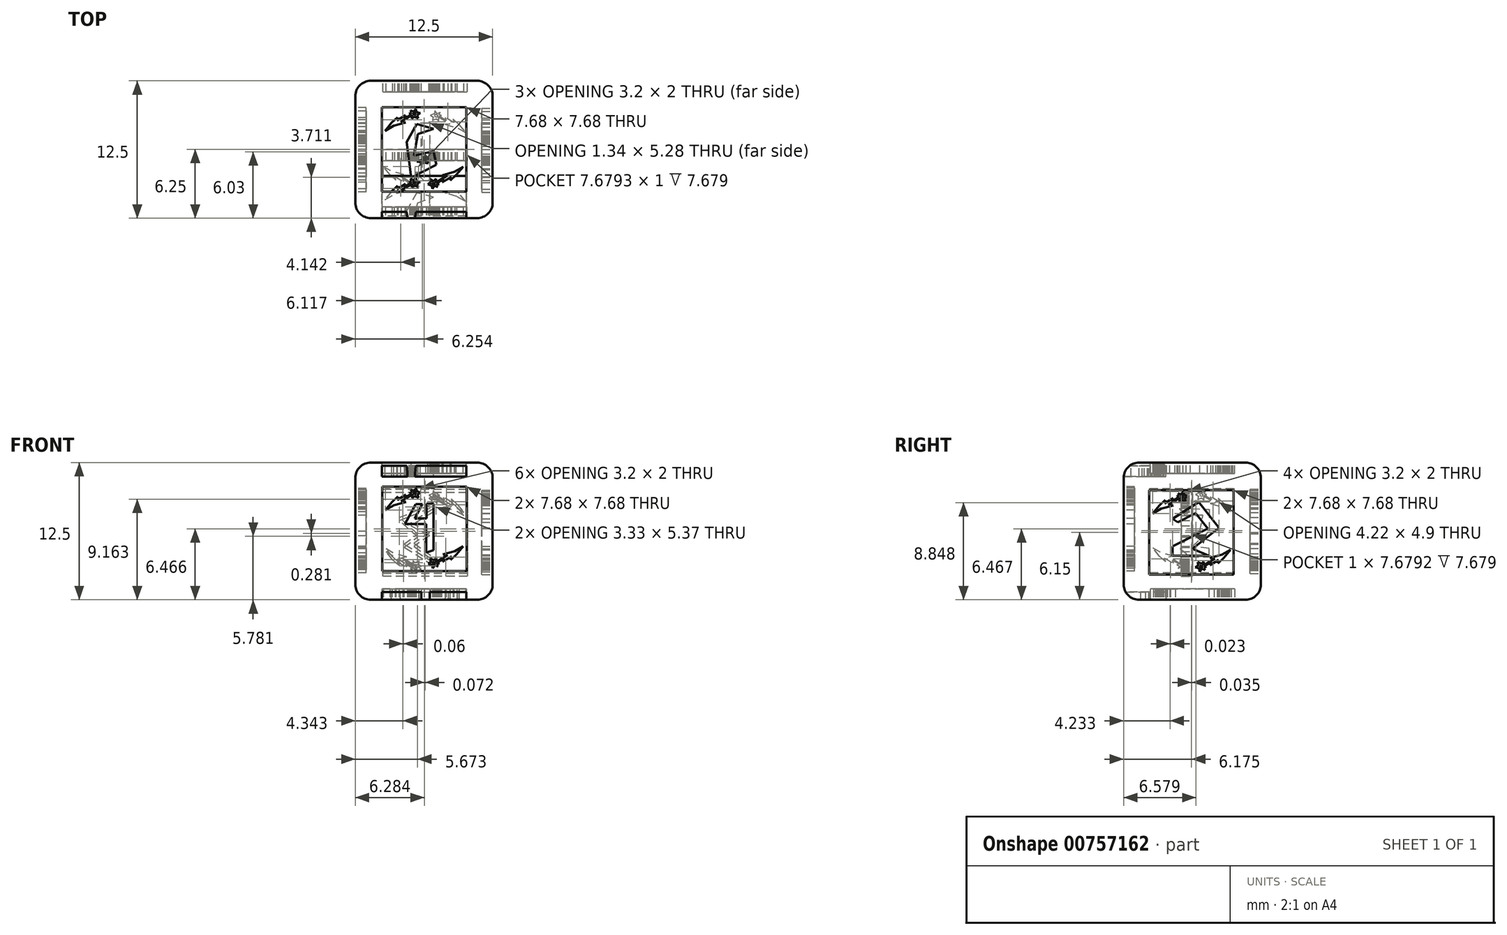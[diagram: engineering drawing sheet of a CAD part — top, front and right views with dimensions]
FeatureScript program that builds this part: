
annotation { "Feature Type Name" : "Feature", "Feature Type Description" : "" }
export const myFeature = defineFeature(function(context is Context, id is Id, definition is map)
    precondition{}
    {
        {
            var Q0;
            Q0=qCreatedBy(makeId("Front.planeOp"),FACE);
            var sketch = newSketch(context, id + "F0", { "sketchPlane" : qUnion([Q0])});
            skLineSegment(sketch, "E0.bottom", {"start": v(-6.25, 5.97) * mm, "end": v(6.25, 5.97) * mm});
            skLineSegment(sketch, "E0.top", {"start": v(-6.25, -6.53) * mm, "end": v(6.25, -6.53) * mm});
            skLineSegment(sketch, "E0.left", {"start": v(-6.25, 5.97) * mm, "end": v(-6.25, -6.53) * mm});
            skLineSegment(sketch, "E0.right", {"start": v(6.25, 5.97) * mm, "end": v(6.25, -6.53) * mm});
            skSolve(sketch);
        }
        {
            var Q0;
            Q0=makeQuery(id+"F0.imprint","IMPRINT",FACE,{"disambiguationData":[TD([[makeQuery(id+"F0.imprint","IMPRINT",EDGE,{"derivedFrom":sQuery(id+"F0.wireOp",EDGE,"E0.bottom")}),-1.0]])]});
            extrude(context, id + "F1", {"entities" : qUnion([Q0]), "depth" : 12.5 * mm, "offsetDistance" : 25.4 * mm});
        }
        {
            var Q0;
            Q0=makeQuery(id+"F1.opExtrude","SWEPT_EDGE",EDGE,{"disambiguationData":[OSD([sQuery(id+"F0.wireOp",EDGE,"E0.bottom"),sQuery(id+"F0.wireOp",EDGE,"E0.left")])]});
            var Q1;
            Q1=makeQuery(id+"F1.opExtrude","SWEPT_FACE",FACE,{"disambiguationData":[OSD([sQuery(id+"F0.wireOp",EDGE,"E0.bottom")])]});
            var Q2;
            Q2=makeQuery(id+"F1.opExtrude","SWEPT_FACE",FACE,{"disambiguationData":[OSD([sQuery(id+"F0.wireOp",EDGE,"E0.top")])]});
            var Q3;
            Q3=makeQuery(id+"F1.opExtrude","CAP_FACE",FACE,{"disambiguationData":[OSD([sQuery(id+"F0.wireOp",EDGE,"E0.bottom"),sQuery(id+"F0.wireOp",EDGE,"E0.top"),sQuery(id+"F0.wireOp",EDGE,"E0.left"),sQuery(id+"F0.wireOp",EDGE,"E0.right")])],"isStart":false});
            var Q4;
            Q4=makeQuery(id+"F1.opExtrude","SWEPT_FACE",FACE,{"disambiguationData":[OSD([sQuery(id+"F0.wireOp",EDGE,"E0.right")])]});
            var Q5;
            Q5=makeQuery(id+"F1.opExtrude","CAP_FACE",FACE,{"disambiguationData":[OSD([sQuery(id+"F0.wireOp",EDGE,"E0.bottom"),sQuery(id+"F0.wireOp",EDGE,"E0.top"),sQuery(id+"F0.wireOp",EDGE,"E0.left"),sQuery(id+"F0.wireOp",EDGE,"E0.right")])],"isStart":true});
            fillet(context, id + "F2", {"entities" : qUnion([Q0, Q1, Q2, Q3, Q4, Q5]), "radius" : 1.41 * mm, "tangentPropagation" : true, "allowEdgeOverflow" : false});
        }
        {
            var Q0;
            Q0=makeQuery(id+"F1.opExtrude","SWEPT_FACE",FACE,{"disambiguationData":[OSD([sQuery(id+"F0.wireOp",EDGE,"E0.bottom")])]});
            var sketch = newSketch(context, id + "F3", { "sketchPlane" : qUnion([Q0])});
            skLineSegment(sketch, "E1.0", {"start": v(3.84, -2.41) * mm, "end": v(-3.84, -2.41) * mm});
            skLineSegment(sketch, "E1.1", {"start": v(3.84, -10.09) * mm, "end": v(3.84, -2.41) * mm});
            skLineSegment(sketch, "E1.2", {"start": v(-3.84, -10.09) * mm, "end": v(3.84, -10.09) * mm});
            skLineSegment(sketch, "E1.3", {"start": v(-3.84, -2.41) * mm, "end": v(-3.84, -10.09) * mm});
            skLineSegment(sketch, "E2", {"start": v(-2.93, -3.8) * mm, "end": v(-2.39, -3.31) * mm});
            skLineSegment(sketch, "E3", {"start": v(-2.39, -3.31) * mm, "end": v(-2.46, -3.62) * mm});
            skLineSegment(sketch, "E4", {"start": v(-2.46, -3.62) * mm, "end": v(-1.66, -3.14) * mm});
            skLineSegment(sketch, "E5", {"start": v(-1.66, -3.14) * mm, "end": v(-1.75, -3.43) * mm});
            skLineSegment(sketch, "E6", {"start": v(-1.75, -3.43) * mm, "end": v(-1.12, -3.06) * mm});
            skLineSegment(sketch, "E7", {"start": v(-1.12, -3.06) * mm, "end": v(-1.35, -3) * mm});
            skLineSegment(sketch, "E8", {"start": v(-1.35, -3) * mm, "end": v(-1.12, -2.88) * mm});
            skLineSegment(sketch, "E9", {"start": v(-1.12, -2.88) * mm, "end": v(-1.22, -2.7) * mm});
            skLineSegment(sketch, "E10", {"start": v(-1.22, -2.7) * mm, "end": v(-0.94, -2.83) * mm});
            skLineSegment(sketch, "E11", {"start": v(-0.94, -2.83) * mm, "end": v(-0.75, -2.55) * mm});
            skLineSegment(sketch, "E12", {"start": v(-0.75, -2.55) * mm, "end": v(-0.68, -2.84) * mm});
            skLineSegment(sketch, "E13", {"start": v(-0.68, -2.84) * mm, "end": v(-0.34, -2.95) * mm});
            skLineSegment(sketch, "E14", {"start": v(-0.34, -2.95) * mm, "end": v(-0.6, -3.12) * mm});
            skLineSegment(sketch, "E15", {"start": v(-0.6, -3.12) * mm, "end": v(-0.54, -3.43) * mm});
            skLineSegment(sketch, "E16", {"start": v(-0.54, -3.43) * mm, "end": v(-0.89, -3.26) * mm});
            skLineSegment(sketch, "E17", {"start": v(-0.89, -3.26) * mm, "end": v(-1.08, -3.47) * mm});
            skLineSegment(sketch, "E18", {"start": v(-1.08, -3.47) * mm, "end": v(-1.08, -3.12) * mm});
            skLineSegment(sketch, "E19", {"start": v(-1.08, -3.12) * mm, "end": v(-2.1, -3.74) * mm});
            skLineSegment(sketch, "E20", {"start": v(-2.1, -3.74) * mm, "end": v(-1.66, -3.8) * mm});
            skLineSegment(sketch, "E21", {"start": v(-1.66, -3.8) * mm, "end": v(-2.75, -4.1) * mm});
            skLineSegment(sketch, "E22", {"start": v(-2.93, -3.8) * mm, "end": v(-3.54, -4.55) * mm});
            skLineSegment(sketch, "E23", {"start": v(-3.54, -4.55) * mm, "end": v(-2.75, -4.1) * mm});
            skLineSegment(sketch, "E24", {"start": v(-0.9, -2.92) * mm, "end": v(-0.77, -2.9) * mm});
            skLineSegment(sketch, "E25", {"start": v(-0.77, -2.9) * mm, "end": v(-0.7, -2.97) * mm});
            skLineSegment(sketch, "E26", {"start": v(-0.7, -2.97) * mm, "end": v(-0.74, -3.08) * mm});
            skLineSegment(sketch, "E27", {"start": v(-0.74, -3.08) * mm, "end": v(-0.9, -3.11) * mm});
            skLineSegment(sketch, "E28", {"start": v(-0.9, -3.11) * mm, "end": v(-1.03, -3.03) * mm});
            skLineSegment(sketch, "E29", {"start": v(-1.03, -3.03) * mm, "end": v(-0.9, -2.92) * mm});
            skLineSegment(sketch, "E30", {"start": v(2.95, -8.58) * mm, "end": v(2.4, -9.07) * mm});
            skLineSegment(sketch, "E31", {"start": v(2.4, -9.07) * mm, "end": v(2.48, -8.76) * mm});
            skLineSegment(sketch, "E32", {"start": v(2.48, -8.76) * mm, "end": v(1.68, -9.24) * mm});
            skLineSegment(sketch, "E33", {"start": v(1.68, -9.24) * mm, "end": v(1.77, -8.96) * mm});
            skLineSegment(sketch, "E34", {"start": v(1.77, -8.96) * mm, "end": v(1.14, -9.33) * mm});
            skLineSegment(sketch, "E35", {"start": v(1.14, -9.33) * mm, "end": v(1.37, -9.38) * mm});
            skLineSegment(sketch, "E36", {"start": v(1.37, -9.38) * mm, "end": v(1.14, -9.5) * mm});
            skLineSegment(sketch, "E37", {"start": v(1.14, -9.5) * mm, "end": v(1.24, -9.69) * mm});
            skLineSegment(sketch, "E38", {"start": v(1.24, -9.69) * mm, "end": v(0.96, -9.56) * mm});
            skLineSegment(sketch, "E39", {"start": v(0.96, -9.56) * mm, "end": v(0.77, -9.83) * mm});
            skLineSegment(sketch, "E40", {"start": v(0.77, -9.83) * mm, "end": v(0.7, -9.54) * mm});
            skLineSegment(sketch, "E41", {"start": v(0.7, -9.54) * mm, "end": v(0.36, -9.43) * mm});
            skLineSegment(sketch, "E42", {"start": v(0.36, -9.43) * mm, "end": v(0.63, -9.26) * mm});
            skLineSegment(sketch, "E43", {"start": v(0.63, -9.26) * mm, "end": v(0.56, -8.95) * mm});
            skLineSegment(sketch, "E44", {"start": v(0.56, -8.95) * mm, "end": v(0.9, -9.12) * mm});
            skLineSegment(sketch, "E45", {"start": v(0.9, -9.12) * mm, "end": v(1.1, -8.92) * mm});
            skLineSegment(sketch, "E46", {"start": v(1.1, -8.92) * mm, "end": v(1.1, -9.27) * mm});
            skLineSegment(sketch, "E47", {"start": v(1.1, -9.27) * mm, "end": v(2.12, -8.64) * mm});
            skLineSegment(sketch, "E48", {"start": v(2.12, -8.64) * mm, "end": v(1.68, -8.59) * mm});
            skLineSegment(sketch, "E49", {"start": v(1.68, -8.59) * mm, "end": v(2.77, -8.3) * mm});
            skLineSegment(sketch, "E50", {"start": v(2.95, -8.58) * mm, "end": v(3.56, -7.83) * mm});
            skLineSegment(sketch, "E51", {"start": v(3.56, -7.83) * mm, "end": v(2.77, -8.3) * mm});
            skLineSegment(sketch, "E52", {"start": v(0.92, -9.47) * mm, "end": v(0.8, -9.49) * mm});
            skLineSegment(sketch, "E53", {"start": v(0.8, -9.49) * mm, "end": v(0.72, -9.41) * mm});
            skLineSegment(sketch, "E54", {"start": v(0.72, -9.41) * mm, "end": v(0.76, -9.3) * mm});
            skLineSegment(sketch, "E55", {"start": v(0.76, -9.3) * mm, "end": v(0.92, -9.27) * mm});
            skLineSegment(sketch, "E56", {"start": v(0.92, -9.27) * mm, "end": v(1.05, -9.35) * mm});
            skLineSegment(sketch, "E57", {"start": v(1.05, -9.35) * mm, "end": v(0.92, -9.47) * mm});
            skLineSegment(sketch, "E58", {"start": v(0.88, -4.36) * mm, "end": v(-0.65, -3.94) * mm});
            skLineSegment(sketch, "E59", {"start": v(-0.65, -3.94) * mm, "end": v(-1.59, -5.58) * mm});
            skLineSegment(sketch, "E60", {"start": v(-1.59, -5.58) * mm, "end": v(-1.17, -8.8) * mm});
            skLineSegment(sketch, "E61", {"start": v(-1.17, -8.8) * mm, "end": v(1.14, -7.65) * mm});
            skLineSegment(sketch, "E62", {"start": v(1.14, -7.65) * mm, "end": v(0.86, -6.41) * mm});
            skLineSegment(sketch, "E63", {"start": v(0.86, -6.41) * mm, "end": v(-0.92, -6.82) * mm});
            skLineSegment(sketch, "E64", {"start": v(-0.92, -6.82) * mm, "end": v(-0.57, -4.86) * mm});
            skLineSegment(sketch, "E65", {"start": v(-0.57, -4.86) * mm, "end": v(0.88, -4.36) * mm});
            skLineSegment(sketch, "E66", {"start": v(0.16, -7.09) * mm, "end": v(-0.66, -7.37) * mm});
            skLineSegment(sketch, "E67", {"start": v(-0.66, -7.37) * mm, "end": v(0.38, -7.53) * mm});
            skLineSegment(sketch, "E68", {"start": v(0.38, -7.53) * mm, "end": v(0.16, -7.09) * mm});
            skSolve(sketch);
        }
        {
            var Q0;
            Q0=makeQuery(id+"F3.imprint","IMPRINT",FACE,{"disambiguationData":[TD([[makeQuery(id+"F3.imprint","IMPRINT",EDGE,{"derivedFrom":sQuery(id+"F3.wireOp",EDGE,"E1.0")}),1.0]])]});
            var Q1;
            Q1=makeQuery(id+"F3.imprint","IMPRINT",FACE,{"disambiguationData":[TD([[makeQuery(id+"F3.imprint","IMPRINT",EDGE,{"derivedFrom":sQuery(id+"F3.wireOp",EDGE,"ba902a5d-1331-4e5e-a22d-ac149d70c835.sketch_text.stroke-17")}),1.0]])]});
            var Q2;
            Q2=makeQuery(id+"F3.imprint","IMPRINT",FACE,{"disambiguationData":[TD([[makeQuery(id+"F3.imprint","IMPRINT",EDGE,{"derivedFrom":sQuery(id+"F3.wireOp",EDGE,"E52")}),-1.0]])]});
            var Q3;
            Q3=makeQuery(id+"F3.imprint","IMPRINT",FACE,{"disambiguationData":[TD([[makeQuery(id+"F3.imprint","IMPRINT",EDGE,{"derivedFrom":sQuery(id+"F3.wireOp",EDGE,"E24")}),-1.0]])]});
            var Q4;
            Q4=makeQuery(id+"F3.imprint","IMPRINT",FACE,{"disambiguationData":[TD([[makeQuery(id+"F3.imprint","IMPRINT",EDGE,{"derivedFrom":sQuery(id+"F3.wireOp",EDGE,"E66")}),1.0]])]});
            extrude(context, id + "F4", {"entities" : qUnion([Q0, Q1, Q2, Q3, Q4]), "operationType" : NewBodyOperationType.REMOVE, "oppositeDirection" : true, "depth" : 1 * mm, "offsetDistance" : 25.4 * mm});
        }
        {
            var Q0;
            Q0=makeQuery(id+"F1.opExtrude","CAP_FACE",FACE,{"disambiguationData":[OSD([sQuery(id+"F0.wireOp",EDGE,"E0.bottom"),sQuery(id+"F0.wireOp",EDGE,"E0.top"),sQuery(id+"F0.wireOp",EDGE,"E0.left"),sQuery(id+"F0.wireOp",EDGE,"E0.right")])],"isStart":true});
            var sketch = newSketch(context, id + "F5", { "sketchPlane" : qUnion([Q0])});
            skLineSegment(sketch, "E69.0", {"start": v(3.73, 3.56) * mm, "end": v(-3.95, 3.56) * mm});
            skLineSegment(sketch, "E69.1", {"start": v(3.73, -4.12) * mm, "end": v(3.73, 3.56) * mm});
            skLineSegment(sketch, "E69.2", {"start": v(-3.95, -4.12) * mm, "end": v(3.73, -4.12) * mm});
            skLineSegment(sketch, "E69.3", {"start": v(-3.95, 3.56) * mm, "end": v(-3.95, -4.12) * mm});
            skLineSegment(sketch, "E70", {"start": v(-3.04, 2.16) * mm, "end": v(-2.5, 2.65) * mm});
            skLineSegment(sketch, "E71", {"start": v(-2.5, 2.65) * mm, "end": v(-2.57, 2.34) * mm});
            skLineSegment(sketch, "E72", {"start": v(-2.57, 2.34) * mm, "end": v(-1.77, 2.82) * mm});
            skLineSegment(sketch, "E73", {"start": v(-1.77, 2.82) * mm, "end": v(-1.86, 2.54) * mm});
            skLineSegment(sketch, "E74", {"start": v(-1.86, 2.54) * mm, "end": v(-1.23, 2.9) * mm});
            skLineSegment(sketch, "E75", {"start": v(-1.23, 2.9) * mm, "end": v(-1.46, 2.96) * mm});
            skLineSegment(sketch, "E76", {"start": v(-1.46, 2.96) * mm, "end": v(-1.23, 3.08) * mm});
            skLineSegment(sketch, "E77", {"start": v(-1.23, 3.08) * mm, "end": v(-1.33, 3.27) * mm});
            skLineSegment(sketch, "E78", {"start": v(-1.33, 3.27) * mm, "end": v(-1.05, 3.14) * mm});
            skLineSegment(sketch, "E79", {"start": v(-1.05, 3.14) * mm, "end": v(-0.86, 3.42) * mm});
            skLineSegment(sketch, "E80", {"start": v(-0.86, 3.42) * mm, "end": v(-0.8, 3.13) * mm});
            skLineSegment(sketch, "E81", {"start": v(-0.8, 3.13) * mm, "end": v(-0.45, 3.01) * mm});
            skLineSegment(sketch, "E82", {"start": v(-0.45, 3.01) * mm, "end": v(-0.72, 2.85) * mm});
            skLineSegment(sketch, "E83", {"start": v(-0.72, 2.85) * mm, "end": v(-0.65, 2.53) * mm});
            skLineSegment(sketch, "E84", {"start": v(-0.65, 2.53) * mm, "end": v(-1, 2.7) * mm});
            skLineSegment(sketch, "E85", {"start": v(-1, 2.7) * mm, "end": v(-1.2, 2.5) * mm});
            skLineSegment(sketch, "E86", {"start": v(-1.2, 2.5) * mm, "end": v(-1.2, 2.85) * mm});
            skLineSegment(sketch, "E87", {"start": v(-1.2, 2.85) * mm, "end": v(-2.2, 2.22) * mm});
            skLineSegment(sketch, "E88", {"start": v(-2.2, 2.22) * mm, "end": v(-1.77, 2.17) * mm});
            skLineSegment(sketch, "E89", {"start": v(-1.77, 2.17) * mm, "end": v(-2.86, 1.87) * mm});
            skLineSegment(sketch, "E90", {"start": v(-3.04, 2.16) * mm, "end": v(-3.65, 1.41) * mm});
            skLineSegment(sketch, "E91", {"start": v(-3.65, 1.41) * mm, "end": v(-2.86, 1.87) * mm});
            skLineSegment(sketch, "E92", {"start": v(-1.01, 3.05) * mm, "end": v(-0.88, 3.07) * mm});
            skLineSegment(sketch, "E93", {"start": v(-0.88, 3.07) * mm, "end": v(-0.81, 3) * mm});
            skLineSegment(sketch, "E94", {"start": v(-0.81, 3) * mm, "end": v(-0.85, 2.88) * mm});
            skLineSegment(sketch, "E95", {"start": v(-0.85, 2.88) * mm, "end": v(-1, 2.86) * mm});
            skLineSegment(sketch, "E96", {"start": v(-1, 2.86) * mm, "end": v(-1.14, 2.94) * mm});
            skLineSegment(sketch, "E97", {"start": v(-1.14, 2.94) * mm, "end": v(-1.01, 3.05) * mm});
            skLineSegment(sketch, "E98", {"start": v(2.84, -2.61) * mm, "end": v(2.3, -3.1) * mm});
            skLineSegment(sketch, "E99", {"start": v(2.3, -3.1) * mm, "end": v(2.37, -2.8) * mm});
            skLineSegment(sketch, "E100", {"start": v(2.37, -2.8) * mm, "end": v(1.57, -3.27) * mm});
            skLineSegment(sketch, "E101", {"start": v(1.57, -3.27) * mm, "end": v(1.66, -3) * mm});
            skLineSegment(sketch, "E102", {"start": v(1.66, -3) * mm, "end": v(1.03, -3.36) * mm});
            skLineSegment(sketch, "E103", {"start": v(1.03, -3.36) * mm, "end": v(1.26, -3.41) * mm});
            skLineSegment(sketch, "E104", {"start": v(1.26, -3.41) * mm, "end": v(1.03, -3.53) * mm});
            skLineSegment(sketch, "E105", {"start": v(1.03, -3.53) * mm, "end": v(1.13, -3.72) * mm});
            skLineSegment(sketch, "E106", {"start": v(1.13, -3.72) * mm, "end": v(0.85, -3.6) * mm});
            skLineSegment(sketch, "E107", {"start": v(0.85, -3.6) * mm, "end": v(0.66, -3.87) * mm});
            skLineSegment(sketch, "E108", {"start": v(0.66, -3.87) * mm, "end": v(0.6, -3.58) * mm});
            skLineSegment(sketch, "E109", {"start": v(0.6, -3.58) * mm, "end": v(0.25, -3.46) * mm});
            skLineSegment(sketch, "E110", {"start": v(0.25, -3.46) * mm, "end": v(0.52, -3.3) * mm});
            skLineSegment(sketch, "E111", {"start": v(0.52, -3.3) * mm, "end": v(0.45, -2.98) * mm});
            skLineSegment(sketch, "E112", {"start": v(0.45, -2.98) * mm, "end": v(0.8, -3.15) * mm});
            skLineSegment(sketch, "E113", {"start": v(0.8, -3.15) * mm, "end": v(1, -2.95) * mm});
            skLineSegment(sketch, "E114", {"start": v(1, -2.95) * mm, "end": v(1, -3.3) * mm});
            skLineSegment(sketch, "E115", {"start": v(1, -3.3) * mm, "end": v(2, -2.67) * mm});
            skLineSegment(sketch, "E116", {"start": v(2, -2.67) * mm, "end": v(1.57, -2.62) * mm});
            skLineSegment(sketch, "E117", {"start": v(1.57, -2.62) * mm, "end": v(2.66, -2.32) * mm});
            skLineSegment(sketch, "E118", {"start": v(2.84, -2.61) * mm, "end": v(3.45, -1.86) * mm});
            skLineSegment(sketch, "E119", {"start": v(3.45, -1.86) * mm, "end": v(2.66, -2.32) * mm});
            skLineSegment(sketch, "E120", {"start": v(0.81, -3.5) * mm, "end": v(0.68, -3.52) * mm});
            skLineSegment(sketch, "E121", {"start": v(0.68, -3.52) * mm, "end": v(0.61, -3.44) * mm});
            skLineSegment(sketch, "E122", {"start": v(0.61, -3.44) * mm, "end": v(0.65, -3.33) * mm});
            skLineSegment(sketch, "E123", {"start": v(0.65, -3.33) * mm, "end": v(0.8, -3.3) * mm});
            skLineSegment(sketch, "E124", {"start": v(0.8, -3.3) * mm, "end": v(0.94, -3.38) * mm});
            skLineSegment(sketch, "E125", {"start": v(0.94, -3.38) * mm, "end": v(0.81, -3.5) * mm});
            skLineSegment(sketch, "E126", {"start": v(-0.85, 2.22) * mm, "end": v(-0.85, 1.73) * mm});
            skLineSegment(sketch, "E127", {"start": v(-0.85, 1.73) * mm, "end": v(1.2, 0.48) * mm});
            skLineSegment(sketch, "E128", {"start": v(1.2, 0.48) * mm, "end": v(-0.53, -0.4) * mm});
            skLineSegment(sketch, "E129", {"start": v(-0.53, -0.4) * mm, "end": v(0.91, -1.38) * mm});
            skLineSegment(sketch, "E130", {"start": v(0.91, -1.38) * mm, "end": v(-1.1, -2.81) * mm});
            skLineSegment(sketch, "E131", {"start": v(-1.1, -2.81) * mm, "end": v(-0.85, -3.15) * mm});
            skLineSegment(sketch, "E132", {"start": v(-0.85, -3.15) * mm, "end": v(1.84, -1.46) * mm});
            skLineSegment(sketch, "E133", {"start": v(1.84, -1.46) * mm, "end": v(0.58, -0.53) * mm});
            skLineSegment(sketch, "E134", {"start": v(0.58, -0.53) * mm, "end": v(2.24, 0.96) * mm});
            skLineSegment(sketch, "E135", {"start": v(2.24, 0.96) * mm, "end": v(-0.85, 2.22) * mm});
            skSolve(sketch);
        }
        {
            var Q0;
            Q0=makeQuery(id+"F5.imprint","IMPRINT",FACE,{"disambiguationData":[TD([[makeQuery(id+"F5.imprint","IMPRINT",EDGE,{"derivedFrom":sQuery(id+"F5.wireOp",EDGE,"E92")}),-1.0]])]});
            var Q1;
            Q1=makeQuery(id+"F5.imprint","IMPRINT",FACE,{"disambiguationData":[TD([[makeQuery(id+"F5.imprint","IMPRINT",EDGE,{"derivedFrom":sQuery(id+"F5.wireOp",EDGE,"E69.0")}),1.0]])]});
            var Q2;
            Q2=makeQuery(id+"F5.imprint","IMPRINT",FACE,{"disambiguationData":[TD([[makeQuery(id+"F5.imprint","IMPRINT",EDGE,{"derivedFrom":sQuery(id+"F5.wireOp",EDGE,"E120")}),-1.0]])]});
            extrude(context, id + "F6", {"entities" : qUnion([Q0, Q1, Q2]), "operationType" : NewBodyOperationType.REMOVE, "oppositeDirection" : true, "depth" : 1 * mm, "offsetDistance" : 25.4 * mm});
        }
        {
            var Q0;
            Q0=makeQuery(id+"F1.opExtrude","SWEPT_FACE",FACE,{"disambiguationData":[OSD([sQuery(id+"F0.wireOp",EDGE,"E0.top")])]});
            var sketch = newSketch(context, id + "F7", { "sketchPlane" : qUnion([Q0])});
            skLineSegment(sketch, "E136.0", {"start": v(3.84, 10.09) * mm, "end": v(-3.84, 10.09) * mm});
            skLineSegment(sketch, "E136.1", {"start": v(3.84, 2.41) * mm, "end": v(3.84, 10.09) * mm});
            skLineSegment(sketch, "E136.2", {"start": v(-3.84, 2.41) * mm, "end": v(3.84, 2.41) * mm});
            skLineSegment(sketch, "E136.3", {"start": v(-3.84, 10.09) * mm, "end": v(-3.84, 2.41) * mm});
            skLineSegment(sketch, "E137", {"start": v(-3.1, 8.53) * mm, "end": v(-2.56, 9.03) * mm});
            skLineSegment(sketch, "E138", {"start": v(-2.56, 9.03) * mm, "end": v(-2.63, 8.72) * mm});
            skLineSegment(sketch, "E139", {"start": v(-2.63, 8.72) * mm, "end": v(-1.83, 9.2) * mm});
            skLineSegment(sketch, "E140", {"start": v(-1.83, 9.2) * mm, "end": v(-1.92, 8.92) * mm});
            skLineSegment(sketch, "E141", {"start": v(-1.92, 8.92) * mm, "end": v(-1.3, 9.28) * mm});
            skLineSegment(sketch, "E142", {"start": v(-1.3, 9.28) * mm, "end": v(-1.52, 9.34) * mm});
            skLineSegment(sketch, "E143", {"start": v(-1.52, 9.34) * mm, "end": v(-1.3, 9.46) * mm});
            skLineSegment(sketch, "E144", {"start": v(-1.3, 9.46) * mm, "end": v(-1.4, 9.65) * mm});
            skLineSegment(sketch, "E145", {"start": v(-1.4, 9.65) * mm, "end": v(-1.11, 9.51) * mm});
            skLineSegment(sketch, "E146", {"start": v(-1.11, 9.51) * mm, "end": v(-0.92, 9.79) * mm});
            skLineSegment(sketch, "E147", {"start": v(-0.92, 9.79) * mm, "end": v(-0.85, 9.5) * mm});
            skLineSegment(sketch, "E148", {"start": v(-0.85, 9.5) * mm, "end": v(-0.5, 9.39) * mm});
            skLineSegment(sketch, "E149", {"start": v(-0.5, 9.39) * mm, "end": v(-0.78, 9.22) * mm});
            skLineSegment(sketch, "E150", {"start": v(-0.78, 9.22) * mm, "end": v(-0.7, 8.9) * mm});
            skLineSegment(sketch, "E151", {"start": v(-0.7, 8.9) * mm, "end": v(-1.06, 9.08) * mm});
            skLineSegment(sketch, "E152", {"start": v(-1.06, 9.08) * mm, "end": v(-1.26, 8.87) * mm});
            skLineSegment(sketch, "E153", {"start": v(-1.26, 8.87) * mm, "end": v(-1.26, 9.23) * mm});
            skLineSegment(sketch, "E154", {"start": v(-1.26, 9.23) * mm, "end": v(-2.27, 8.6) * mm});
            skLineSegment(sketch, "E155", {"start": v(-2.27, 8.6) * mm, "end": v(-1.83, 8.54) * mm});
            skLineSegment(sketch, "E156", {"start": v(-1.83, 8.54) * mm, "end": v(-2.92, 8.25) * mm});
            skLineSegment(sketch, "E157", {"start": v(-3.1, 8.53) * mm, "end": v(-3.7, 7.79) * mm});
            skLineSegment(sketch, "E158", {"start": v(-3.7, 7.79) * mm, "end": v(-2.92, 8.25) * mm});
            skLineSegment(sketch, "E159", {"start": v(-1.08, 9.43) * mm, "end": v(-0.94, 9.45) * mm});
            skLineSegment(sketch, "E160", {"start": v(-0.94, 9.45) * mm, "end": v(-0.87, 9.37) * mm});
            skLineSegment(sketch, "E161", {"start": v(-0.87, 9.37) * mm, "end": v(-0.91, 9.26) * mm});
            skLineSegment(sketch, "E162", {"start": v(-0.91, 9.26) * mm, "end": v(-1.07, 9.23) * mm});
            skLineSegment(sketch, "E163", {"start": v(-1.07, 9.23) * mm, "end": v(-1.2, 9.3) * mm});
            skLineSegment(sketch, "E164", {"start": v(-1.2, 9.3) * mm, "end": v(-1.08, 9.43) * mm});
            skLineSegment(sketch, "E165", {"start": v(3.18, 3.98) * mm, "end": v(2.64, 3.49) * mm});
            skLineSegment(sketch, "E166", {"start": v(2.64, 3.49) * mm, "end": v(2.71, 3.8) * mm});
            skLineSegment(sketch, "E167", {"start": v(2.71, 3.8) * mm, "end": v(1.9, 3.32) * mm});
            skLineSegment(sketch, "E168", {"start": v(1.9, 3.32) * mm, "end": v(2, 3.6) * mm});
            skLineSegment(sketch, "E169", {"start": v(2, 3.6) * mm, "end": v(1.37, 3.23) * mm});
            skLineSegment(sketch, "E170", {"start": v(1.37, 3.23) * mm, "end": v(1.6, 3.18) * mm});
            skLineSegment(sketch, "E171", {"start": v(1.6, 3.18) * mm, "end": v(1.37, 3.06) * mm});
            skLineSegment(sketch, "E172", {"start": v(1.37, 3.06) * mm, "end": v(1.47, 2.87) * mm});
            skLineSegment(sketch, "E173", {"start": v(1.47, 2.87) * mm, "end": v(1.2, 3) * mm});
            skLineSegment(sketch, "E174", {"start": v(1.2, 3) * mm, "end": v(1, 2.73) * mm});
            skLineSegment(sketch, "E175", {"start": v(1, 2.73) * mm, "end": v(0.93, 3.01) * mm});
            skLineSegment(sketch, "E176", {"start": v(0.93, 3.01) * mm, "end": v(0.59, 3.13) * mm});
            skLineSegment(sketch, "E177", {"start": v(0.59, 3.13) * mm, "end": v(0.86, 3.3) * mm});
            skLineSegment(sketch, "E178", {"start": v(0.86, 3.3) * mm, "end": v(0.79, 3.6) * mm});
            skLineSegment(sketch, "E179", {"start": v(0.79, 3.6) * mm, "end": v(1.14, 3.44) * mm});
            skLineSegment(sketch, "E180", {"start": v(1.14, 3.44) * mm, "end": v(1.34, 3.64) * mm});
            skLineSegment(sketch, "E181", {"start": v(1.34, 3.64) * mm, "end": v(1.34, 3.29) * mm});
            skLineSegment(sketch, "E182", {"start": v(1.34, 3.29) * mm, "end": v(2.35, 3.92) * mm});
            skLineSegment(sketch, "E183", {"start": v(2.35, 3.92) * mm, "end": v(1.91, 3.97) * mm});
            skLineSegment(sketch, "E184", {"start": v(1.91, 3.97) * mm, "end": v(3, 4.27) * mm});
            skLineSegment(sketch, "E185", {"start": v(3.18, 3.98) * mm, "end": v(3.79, 4.73) * mm});
            skLineSegment(sketch, "E186", {"start": v(3.79, 4.73) * mm, "end": v(3, 4.27) * mm});
            skLineSegment(sketch, "E187", {"start": v(1.16, 3.09) * mm, "end": v(1.02, 3.07) * mm});
            skLineSegment(sketch, "E188", {"start": v(1.02, 3.07) * mm, "end": v(0.95, 3.15) * mm});
            skLineSegment(sketch, "E189", {"start": v(0.95, 3.15) * mm, "end": v(1, 3.26) * mm});
            skLineSegment(sketch, "E190", {"start": v(1, 3.26) * mm, "end": v(1.15, 3.29) * mm});
            skLineSegment(sketch, "E191", {"start": v(1.15, 3.29) * mm, "end": v(1.28, 3.2) * mm});
            skLineSegment(sketch, "E192", {"start": v(1.28, 3.2) * mm, "end": v(1.16, 3.09) * mm});
            skLineSegment(sketch, "E193", {"start": v(-0.8, 8.3) * mm, "end": v(-0.23, 8.3) * mm});
            skLineSegment(sketch, "E194", {"start": v(-0.23, 8.3) * mm, "end": v(-0.23, 3.83) * mm});
            skLineSegment(sketch, "E195", {"start": v(-0.23, 3.83) * mm, "end": v(0.54, 3.83) * mm});
            skLineSegment(sketch, "E196", {"start": v(0.54, 3.83) * mm, "end": v(0.54, 9.1) * mm});
            skLineSegment(sketch, "E197", {"start": v(0.54, 9.1) * mm, "end": v(0, 9.1) * mm});
            skLineSegment(sketch, "E198", {"start": v(0, 9.1) * mm, "end": v(-0.8, 8.3) * mm});
            skSolve(sketch);
        }
        {
            var Q0;
            Q0=makeQuery(id+"F7.imprint","IMPRINT",FACE,{"disambiguationData":[TD([[makeQuery(id+"F7.imprint","IMPRINT",EDGE,{"derivedFrom":sQuery(id+"F7.wireOp",EDGE,"E136.0")}),1.0]])]});
            var Q1;
            Q1=makeQuery(id+"F7.imprint","IMPRINT",FACE,{"disambiguationData":[TD([[makeQuery(id+"F7.imprint","IMPRINT",EDGE,{"derivedFrom":sQuery(id+"F7.wireOp",EDGE,"E159")}),-1.0]])]});
            var Q2;
            Q2=makeQuery(id+"F7.imprint","IMPRINT",FACE,{"disambiguationData":[TD([[makeQuery(id+"F7.imprint","IMPRINT",EDGE,{"derivedFrom":sQuery(id+"F7.wireOp",EDGE,"E187")}),-1.0]])]});
            extrude(context, id + "F8", {"entities" : qUnion([Q0, Q1, Q2]), "operationType" : NewBodyOperationType.REMOVE, "oppositeDirection" : true, "depth" : 1 * mm, "offsetDistance" : 25.4 * mm});
        }
        {
            var Q0;
            Q0=makeQuery(id+"F1.opExtrude","CAP_FACE",FACE,{"disambiguationData":[OSD([sQuery(id+"F0.wireOp",EDGE,"E0.bottom"),sQuery(id+"F0.wireOp",EDGE,"E0.top"),sQuery(id+"F0.wireOp",EDGE,"E0.left"),sQuery(id+"F0.wireOp",EDGE,"E0.right")])],"isStart":false});
            var sketch = newSketch(context, id + "F9", { "sketchPlane" : qUnion([Q0])});
            skLineSegment(sketch, "E199.0", {"start": v(3.87, 3.78) * mm, "end": v(-3.8, 3.78) * mm});
            skLineSegment(sketch, "E199.1", {"start": v(3.87, -3.9) * mm, "end": v(3.87, 3.78) * mm});
            skLineSegment(sketch, "E199.2", {"start": v(-3.8, -3.9) * mm, "end": v(3.87, -3.9) * mm});
            skLineSegment(sketch, "E199.3", {"start": v(-3.8, 3.78) * mm, "end": v(-3.8, -3.9) * mm});
            skLineSegment(sketch, "E200", {"start": v(-2.9, 2.38) * mm, "end": v(-2.36, 2.87) * mm});
            skLineSegment(sketch, "E201", {"start": v(-2.36, 2.87) * mm, "end": v(-2.43, 2.56) * mm});
            skLineSegment(sketch, "E202", {"start": v(-2.43, 2.56) * mm, "end": v(-1.62, 3.04) * mm});
            skLineSegment(sketch, "E203", {"start": v(-1.62, 3.04) * mm, "end": v(-1.72, 2.76) * mm});
            skLineSegment(sketch, "E204", {"start": v(-1.72, 2.76) * mm, "end": v(-1.09, 3.13) * mm});
            skLineSegment(sketch, "E205", {"start": v(-1.09, 3.13) * mm, "end": v(-1.31, 3.18) * mm});
            skLineSegment(sketch, "E206", {"start": v(-1.31, 3.18) * mm, "end": v(-1.09, 3.3) * mm});
            skLineSegment(sketch, "E207", {"start": v(-1.09, 3.3) * mm, "end": v(-1.19, 3.49) * mm});
            skLineSegment(sketch, "E208", {"start": v(-1.19, 3.49) * mm, "end": v(-0.91, 3.36) * mm});
            skLineSegment(sketch, "E209", {"start": v(-0.91, 3.36) * mm, "end": v(-0.72, 3.63) * mm});
            skLineSegment(sketch, "E210", {"start": v(-0.72, 3.63) * mm, "end": v(-0.65, 3.34) * mm});
            skLineSegment(sketch, "E211", {"start": v(-0.65, 3.34) * mm, "end": v(-0.3, 3.23) * mm});
            skLineSegment(sketch, "E212", {"start": v(-0.3, 3.23) * mm, "end": v(-0.58, 3.06) * mm});
            skLineSegment(sketch, "E213", {"start": v(-0.58, 3.06) * mm, "end": v(-0.5, 2.75) * mm});
            skLineSegment(sketch, "E214", {"start": v(-0.5, 2.75) * mm, "end": v(-0.86, 2.92) * mm});
            skLineSegment(sketch, "E215", {"start": v(-0.86, 2.92) * mm, "end": v(-1.05, 2.72) * mm});
            skLineSegment(sketch, "E216", {"start": v(-1.05, 2.72) * mm, "end": v(-1.05, 3.07) * mm});
            skLineSegment(sketch, "E217", {"start": v(-1.05, 3.07) * mm, "end": v(-2.07, 2.44) * mm});
            skLineSegment(sketch, "E218", {"start": v(-2.07, 2.44) * mm, "end": v(-1.63, 2.39) * mm});
            skLineSegment(sketch, "E219", {"start": v(-1.63, 2.39) * mm, "end": v(-2.72, 2.1) * mm});
            skLineSegment(sketch, "E220", {"start": v(-2.9, 2.38) * mm, "end": v(-3.5, 1.63) * mm});
            skLineSegment(sketch, "E221", {"start": v(-3.5, 1.63) * mm, "end": v(-2.72, 2.1) * mm});
            skLineSegment(sketch, "E222", {"start": v(-0.87, 3.27) * mm, "end": v(-0.74, 3.29) * mm});
            skLineSegment(sketch, "E223", {"start": v(-0.74, 3.29) * mm, "end": v(-0.67, 3.21) * mm});
            skLineSegment(sketch, "E224", {"start": v(-0.67, 3.21) * mm, "end": v(-0.71, 3.1) * mm});
            skLineSegment(sketch, "E225", {"start": v(-0.71, 3.1) * mm, "end": v(-0.87, 3.07) * mm});
            skLineSegment(sketch, "E226", {"start": v(-0.87, 3.07) * mm, "end": v(-1, 3.15) * mm});
            skLineSegment(sketch, "E227", {"start": v(-1, 3.15) * mm, "end": v(-0.87, 3.27) * mm});
            skLineSegment(sketch, "E228", {"start": v(2.98, -2.4) * mm, "end": v(2.44, -2.89) * mm});
            skLineSegment(sketch, "E229", {"start": v(2.44, -2.89) * mm, "end": v(2.5, -2.58) * mm});
            skLineSegment(sketch, "E230", {"start": v(2.5, -2.58) * mm, "end": v(1.7, -3.06) * mm});
            skLineSegment(sketch, "E231", {"start": v(1.7, -3.06) * mm, "end": v(1.8, -2.77) * mm});
            skLineSegment(sketch, "E232", {"start": v(1.8, -2.77) * mm, "end": v(1.17, -3.14) * mm});
            skLineSegment(sketch, "E233", {"start": v(1.17, -3.14) * mm, "end": v(1.4, -3.2) * mm});
            skLineSegment(sketch, "E234", {"start": v(1.4, -3.2) * mm, "end": v(1.17, -3.32) * mm});
            skLineSegment(sketch, "E235", {"start": v(1.17, -3.32) * mm, "end": v(1.27, -3.5) * mm});
            skLineSegment(sketch, "E236", {"start": v(1.27, -3.5) * mm, "end": v(1, -3.37) * mm});
            skLineSegment(sketch, "E237", {"start": v(1, -3.37) * mm, "end": v(0.8, -3.65) * mm});
            skLineSegment(sketch, "E238", {"start": v(0.8, -3.65) * mm, "end": v(0.73, -3.36) * mm});
            skLineSegment(sketch, "E239", {"start": v(0.73, -3.36) * mm, "end": v(0.39, -3.25) * mm});
            skLineSegment(sketch, "E240", {"start": v(0.39, -3.25) * mm, "end": v(0.66, -3.08) * mm});
            skLineSegment(sketch, "E241", {"start": v(0.66, -3.08) * mm, "end": v(0.59, -2.77) * mm});
            skLineSegment(sketch, "E242", {"start": v(0.59, -2.77) * mm, "end": v(0.94, -2.94) * mm});
            skLineSegment(sketch, "E243", {"start": v(0.94, -2.94) * mm, "end": v(1.14, -2.73) * mm});
            skLineSegment(sketch, "E244", {"start": v(1.14, -2.73) * mm, "end": v(1.14, -3.08) * mm});
            skLineSegment(sketch, "E245", {"start": v(1.14, -3.08) * mm, "end": v(2.15, -2.46) * mm});
            skLineSegment(sketch, "E246", {"start": v(2.15, -2.46) * mm, "end": v(1.71, -2.4) * mm});
            skLineSegment(sketch, "E247", {"start": v(1.71, -2.4) * mm, "end": v(2.8, -2.1) * mm});
            skLineSegment(sketch, "E248", {"start": v(2.98, -2.4) * mm, "end": v(3.59, -1.65) * mm});
            skLineSegment(sketch, "E249", {"start": v(3.59, -1.65) * mm, "end": v(2.8, -2.1) * mm});
            skLineSegment(sketch, "E250", {"start": v(0.95, -3.28) * mm, "end": v(0.82, -3.3) * mm});
            skLineSegment(sketch, "E251", {"start": v(0.82, -3.3) * mm, "end": v(0.75, -3.23) * mm});
            skLineSegment(sketch, "E252", {"start": v(0.75, -3.23) * mm, "end": v(0.8, -3.11) * mm});
            skLineSegment(sketch, "E253", {"start": v(0.8, -3.11) * mm, "end": v(0.95, -3.09) * mm});
            skLineSegment(sketch, "E254", {"start": v(0.95, -3.09) * mm, "end": v(1.08, -3.17) * mm});
            skLineSegment(sketch, "E255", {"start": v(1.08, -3.17) * mm, "end": v(0.95, -3.28) * mm});
            skLineSegment(sketch, "E256", {"start": v(-0.75, 2.17) * mm, "end": v(-1.74, 0.37) * mm});
            skLineSegment(sketch, "E257", {"start": v(-1.74, 0.37) * mm, "end": v(0.2, 0.37) * mm});
            skLineSegment(sketch, "E258", {"start": v(0.2, 0.37) * mm, "end": v(0.2, -2.22) * mm});
            skLineSegment(sketch, "E259", {"start": v(0.2, -2.22) * mm, "end": v(0.87, -2.01) * mm});
            skLineSegment(sketch, "E260", {"start": v(0.87, -2.01) * mm, "end": v(0.87, 2.22) * mm});
            skLineSegment(sketch, "E261", {"start": v(0.24, 0.9) * mm, "end": v(-0.85, 0.9) * mm});
            skLineSegment(sketch, "E262", {"start": v(-0.85, 0.9) * mm, "end": v(-0.16, 2.17) * mm});
            skLineSegment(sketch, "E263", {"start": v(-0.16, 2.17) * mm, "end": v(-0.75, 2.17) * mm});
            skLineSegment(sketch, "E264", {"start": v(0.24, 0.9) * mm, "end": v(0.24, 2.22) * mm});
            skLineSegment(sketch, "E265", {"start": v(0.24, 2.22) * mm, "end": v(0.87, 2.22) * mm});
            skSolve(sketch);
        }
        {
            var Q0;
            Q0=makeQuery(id+"F9.imprint","IMPRINT",FACE,{"disambiguationData":[TD([[makeQuery(id+"F9.imprint","IMPRINT",EDGE,{"derivedFrom":sQuery(id+"F9.wireOp",EDGE,"E199.0")}),1.0]])]});
            var Q1;
            Q1=makeQuery(id+"F9.imprint","IMPRINT",FACE,{"disambiguationData":[TD([[makeQuery(id+"F9.imprint","IMPRINT",EDGE,{"derivedFrom":sQuery(id+"F9.wireOp",EDGE,"E222")}),-1.0]])]});
            var Q2;
            Q2=makeQuery(id+"F9.imprint","IMPRINT",FACE,{"disambiguationData":[TD([[makeQuery(id+"F9.imprint","IMPRINT",EDGE,{"derivedFrom":sQuery(id+"F9.wireOp",EDGE,"E250")}),-1.0]])]});
            extrude(context, id + "F10", {"entities" : qUnion([Q0, Q1, Q2]), "operationType" : NewBodyOperationType.REMOVE, "oppositeDirection" : true, "depth" : 1 * mm, "offsetDistance" : 25.4 * mm});
        }
        {
            var Q0;
            Q0=makeQuery(id+"F1.opExtrude","SWEPT_BODY",BODY,{"disambiguationData":[OSD([sQuery(id+"F0.wireOp",EDGE,"E0.bottom"),sQuery(id+"F0.wireOp",EDGE,"E0.top"),sQuery(id+"F0.wireOp",EDGE,"E0.left"),sQuery(id+"F0.wireOp",EDGE,"E0.right")])]});
            transform(context, id + "F11", {"entities" : qUnion([Q0]), "transformType" : TransformType.TRANSLATION_3D, "dx" : 0 * mm, "dy" : 6.25 * mm, "dz" : 0.28 * mm, "makeCopy" : false});
        }
        {
            var Q0;
            Q0=makeQuery(id+"F1.opExtrude","SWEPT_FACE",FACE,{"disambiguationData":[OSD([sQuery(id+"F0.wireOp",EDGE,"E0.right")])]});
            var sketch = newSketch(context, id + "F12", { "sketchPlane" : qUnion([Q0])});
            skLineSegment(sketch, "E266.0", {"start": v(3.76, 3.74) * mm, "end": v(-3.92, 3.74) * mm});
            skLineSegment(sketch, "E266.1", {"start": v(3.76, -3.94) * mm, "end": v(3.76, 3.74) * mm});
            skLineSegment(sketch, "E266.2", {"start": v(-3.92, -3.94) * mm, "end": v(3.76, -3.94) * mm});
            skLineSegment(sketch, "E266.3", {"start": v(-3.92, 3.74) * mm, "end": v(-3.92, -3.94) * mm});
            skLineSegment(sketch, "E267", {"start": v(-3.01, 2.34) * mm, "end": v(-2.47, 2.84) * mm});
            skLineSegment(sketch, "E268", {"start": v(-2.47, 2.84) * mm, "end": v(-2.54, 2.53) * mm});
            skLineSegment(sketch, "E269", {"start": v(-2.54, 2.53) * mm, "end": v(-1.73, 3) * mm});
            skLineSegment(sketch, "E270", {"start": v(-1.73, 3) * mm, "end": v(-1.83, 2.72) * mm});
            skLineSegment(sketch, "E271", {"start": v(-1.83, 2.72) * mm, "end": v(-1.2, 3.1) * mm});
            skLineSegment(sketch, "E272", {"start": v(-1.2, 3.1) * mm, "end": v(-1.42, 3.15) * mm});
            skLineSegment(sketch, "E273", {"start": v(-1.42, 3.15) * mm, "end": v(-1.2, 3.27) * mm});
            skLineSegment(sketch, "E274", {"start": v(-1.2, 3.27) * mm, "end": v(-1.3, 3.45) * mm});
            skLineSegment(sketch, "E275", {"start": v(-1.3, 3.45) * mm, "end": v(-1.02, 3.32) * mm});
            skLineSegment(sketch, "E276", {"start": v(-1.02, 3.32) * mm, "end": v(-0.83, 3.6) * mm});
            skLineSegment(sketch, "E277", {"start": v(-0.83, 3.6) * mm, "end": v(-0.76, 3.3) * mm});
            skLineSegment(sketch, "E278", {"start": v(-0.76, 3.3) * mm, "end": v(-0.42, 3.2) * mm});
            skLineSegment(sketch, "E279", {"start": v(-0.42, 3.2) * mm, "end": v(-0.69, 3.03) * mm});
            skLineSegment(sketch, "E280", {"start": v(-0.69, 3.03) * mm, "end": v(-0.61, 2.72) * mm});
            skLineSegment(sketch, "E281", {"start": v(-0.61, 2.72) * mm, "end": v(-0.97, 2.89) * mm});
            skLineSegment(sketch, "E282", {"start": v(-0.97, 2.89) * mm, "end": v(-1.16, 2.68) * mm});
            skLineSegment(sketch, "E283", {"start": v(-1.16, 2.68) * mm, "end": v(-1.16, 3.03) * mm});
            skLineSegment(sketch, "E284", {"start": v(-1.16, 3.03) * mm, "end": v(-2.18, 2.4) * mm});
            skLineSegment(sketch, "E285", {"start": v(-2.18, 2.4) * mm, "end": v(-1.74, 2.35) * mm});
            skLineSegment(sketch, "E286", {"start": v(-1.74, 2.35) * mm, "end": v(-2.83, 2.05) * mm});
            skLineSegment(sketch, "E287", {"start": v(-3.01, 2.34) * mm, "end": v(-3.62, 1.6) * mm});
            skLineSegment(sketch, "E288", {"start": v(-3.62, 1.6) * mm, "end": v(-2.83, 2.05) * mm});
            skLineSegment(sketch, "E289", {"start": v(-0.98, 3.23) * mm, "end": v(-0.85, 3.25) * mm});
            skLineSegment(sketch, "E290", {"start": v(-0.85, 3.25) * mm, "end": v(-0.78, 3.18) * mm});
            skLineSegment(sketch, "E291", {"start": v(-0.78, 3.18) * mm, "end": v(-0.82, 3.07) * mm});
            skLineSegment(sketch, "E292", {"start": v(-0.82, 3.07) * mm, "end": v(-0.98, 3.04) * mm});
            skLineSegment(sketch, "E293", {"start": v(-0.98, 3.04) * mm, "end": v(-1.1, 3.12) * mm});
            skLineSegment(sketch, "E294", {"start": v(-1.1, 3.12) * mm, "end": v(-0.98, 3.23) * mm});
            skLineSegment(sketch, "E295", {"start": v(2.87, -2.43) * mm, "end": v(2.33, -2.92) * mm});
            skLineSegment(sketch, "E296", {"start": v(2.33, -2.92) * mm, "end": v(2.4, -2.61) * mm});
            skLineSegment(sketch, "E297", {"start": v(2.4, -2.61) * mm, "end": v(1.6, -3.1) * mm});
            skLineSegment(sketch, "E298", {"start": v(1.6, -3.1) * mm, "end": v(1.7, -2.8) * mm});
            skLineSegment(sketch, "E299", {"start": v(1.7, -2.8) * mm, "end": v(1.06, -3.18) * mm});
            skLineSegment(sketch, "E300", {"start": v(1.06, -3.18) * mm, "end": v(1.29, -3.23) * mm});
            skLineSegment(sketch, "E301", {"start": v(1.29, -3.23) * mm, "end": v(1.06, -3.35) * mm});
            skLineSegment(sketch, "E302", {"start": v(1.06, -3.35) * mm, "end": v(1.16, -3.54) * mm});
            skLineSegment(sketch, "E303", {"start": v(1.16, -3.54) * mm, "end": v(0.88, -3.4) * mm});
            skLineSegment(sketch, "E304", {"start": v(0.88, -3.4) * mm, "end": v(0.69, -3.68) * mm});
            skLineSegment(sketch, "E305", {"start": v(0.69, -3.68) * mm, "end": v(0.62, -3.4) * mm});
            skLineSegment(sketch, "E306", {"start": v(0.62, -3.4) * mm, "end": v(0.28, -3.28) * mm});
            skLineSegment(sketch, "E307", {"start": v(0.28, -3.28) * mm, "end": v(0.55, -3.11) * mm});
            skLineSegment(sketch, "E308", {"start": v(0.55, -3.11) * mm, "end": v(0.48, -2.8) * mm});
            skLineSegment(sketch, "E309", {"start": v(0.48, -2.8) * mm, "end": v(0.83, -2.97) * mm});
            skLineSegment(sketch, "E310", {"start": v(0.83, -2.97) * mm, "end": v(1.03, -2.77) * mm});
            skLineSegment(sketch, "E311", {"start": v(1.03, -2.77) * mm, "end": v(1.03, -3.12) * mm});
            skLineSegment(sketch, "E312", {"start": v(1.03, -3.12) * mm, "end": v(2.04, -2.5) * mm});
            skLineSegment(sketch, "E313", {"start": v(2.04, -2.5) * mm, "end": v(1.6, -2.44) * mm});
            skLineSegment(sketch, "E314", {"start": v(1.6, -2.44) * mm, "end": v(2.69, -2.14) * mm});
            skLineSegment(sketch, "E315", {"start": v(2.87, -2.43) * mm, "end": v(3.48, -1.68) * mm});
            skLineSegment(sketch, "E316", {"start": v(3.48, -1.68) * mm, "end": v(2.69, -2.14) * mm});
            skLineSegment(sketch, "E317", {"start": v(0.84, -3.32) * mm, "end": v(0.71, -3.34) * mm});
            skLineSegment(sketch, "E318", {"start": v(0.71, -3.34) * mm, "end": v(0.64, -3.26) * mm});
            skLineSegment(sketch, "E319", {"start": v(0.64, -3.26) * mm, "end": v(0.68, -3.15) * mm});
            skLineSegment(sketch, "E320", {"start": v(0.68, -3.15) * mm, "end": v(0.84, -3.12) * mm});
            skLineSegment(sketch, "E321", {"start": v(0.84, -3.12) * mm, "end": v(0.97, -3.2) * mm});
            skLineSegment(sketch, "E322", {"start": v(0.97, -3.2) * mm, "end": v(0.84, -3.32) * mm});
            skLineSegment(sketch, "E323", {"start": v(-1.78, 1.13) * mm, "end": v(-1.33, 0.82) * mm});
            skLineSegment(sketch, "E324", {"start": v(-1.33, 0.82) * mm, "end": v(0.3, 1.65) * mm});
            skLineSegment(sketch, "E325", {"start": v(0.3, 1.65) * mm, "end": v(1.42, 0.25) * mm});
            skLineSegment(sketch, "E326", {"start": v(1.42, 0.25) * mm, "end": v(-1.78, -1.38) * mm});
            skLineSegment(sketch, "E327", {"start": v(-1.78, -1.38) * mm, "end": v(-1.78, -2.23) * mm});
            skLineSegment(sketch, "E328", {"start": v(-1.78, -2.23) * mm, "end": v(1.51, -2.23) * mm});
            skLineSegment(sketch, "E329", {"start": v(1.51, -2.23) * mm, "end": v(0, -1.6) * mm});
            skLineSegment(sketch, "E330", {"start": v(0, -1.6) * mm, "end": v(2.44, 0.3) * mm});
            skLineSegment(sketch, "E331", {"start": v(2.44, 0.3) * mm, "end": v(0.6, 2.67) * mm});
            skLineSegment(sketch, "E332", {"start": v(0.6, 2.67) * mm, "end": v(-1.78, 1.13) * mm});
            skSolve(sketch);
        }
        {
            var Q0;
            Q0=makeQuery(id+"F12.imprint","IMPRINT",FACE,{"disambiguationData":[TD([[makeQuery(id+"F12.imprint","IMPRINT",EDGE,{"derivedFrom":sQuery(id+"F12.wireOp",EDGE,"E266.0")}),1.0]])]});
            var Q1;
            Q1=makeQuery(id+"F12.imprint","IMPRINT",FACE,{"disambiguationData":[TD([[makeQuery(id+"F12.imprint","IMPRINT",EDGE,{"derivedFrom":sQuery(id+"F12.wireOp",EDGE,"E289")}),-1.0]])]});
            var Q2;
            Q2=makeQuery(id+"F12.imprint","IMPRINT",FACE,{"disambiguationData":[TD([[makeQuery(id+"F12.imprint","IMPRINT",EDGE,{"derivedFrom":sQuery(id+"F12.wireOp",EDGE,"E317")}),-1.0]])]});
            extrude(context, id + "F13", {"entities" : qUnion([Q0, Q1, Q2]), "operationType" : NewBodyOperationType.REMOVE, "surfaceOperationType" : NewSurfaceOperationType.ADD, "oppositeDirection" : true, "depth" : 1 * mm, "offsetDistance" : 25.4 * mm});
        }
        {
            var Q0;
            Q0=makeQuery(id+"F1.opExtrude","SWEPT_FACE",FACE,{"disambiguationData":[OSD([sQuery(id+"F0.wireOp",EDGE,"E0.left")])]});
            var sketch = newSketch(context, id + "F14", { "sketchPlane" : qUnion([Q0])});
            skLineSegment(sketch, "E333.0", {"start": v(3.88, 3.9) * mm, "end": v(-3.8, 3.9) * mm});
            skLineSegment(sketch, "E333.1", {"start": v(3.88, -3.78) * mm, "end": v(3.88, 3.9) * mm});
            skLineSegment(sketch, "E333.2", {"start": v(-3.8, -3.78) * mm, "end": v(3.88, -3.78) * mm});
            skLineSegment(sketch, "E333.3", {"start": v(-3.8, 3.9) * mm, "end": v(-3.8, -3.78) * mm});
            skLineSegment(sketch, "E334", {"start": v(-2.9, 2.5) * mm, "end": v(-2.35, 3) * mm});
            skLineSegment(sketch, "E335", {"start": v(-2.35, 3) * mm, "end": v(-2.42, 2.69) * mm});
            skLineSegment(sketch, "E336", {"start": v(-2.42, 2.69) * mm, "end": v(-1.62, 3.17) * mm});
            skLineSegment(sketch, "E337", {"start": v(-1.62, 3.17) * mm, "end": v(-1.72, 2.89) * mm});
            skLineSegment(sketch, "E338", {"start": v(-1.72, 2.89) * mm, "end": v(-1.08, 3.25) * mm});
            skLineSegment(sketch, "E339", {"start": v(-1.08, 3.25) * mm, "end": v(-1.3, 3.3) * mm});
            skLineSegment(sketch, "E340", {"start": v(-1.3, 3.3) * mm, "end": v(-1.08, 3.43) * mm});
            skLineSegment(sketch, "E341", {"start": v(-1.08, 3.43) * mm, "end": v(-1.18, 3.62) * mm});
            skLineSegment(sketch, "E342", {"start": v(-1.18, 3.62) * mm, "end": v(-0.9, 3.49) * mm});
            skLineSegment(sketch, "E343", {"start": v(-0.9, 3.49) * mm, "end": v(-0.7, 3.76) * mm});
            skLineSegment(sketch, "E344", {"start": v(-0.7, 3.76) * mm, "end": v(-0.65, 3.47) * mm});
            skLineSegment(sketch, "E345", {"start": v(-0.65, 3.47) * mm, "end": v(-0.3, 3.36) * mm});
            skLineSegment(sketch, "E346", {"start": v(-0.3, 3.36) * mm, "end": v(-0.57, 3.19) * mm});
            skLineSegment(sketch, "E347", {"start": v(-0.57, 3.19) * mm, "end": v(-0.5, 2.88) * mm});
            skLineSegment(sketch, "E348", {"start": v(-0.5, 2.88) * mm, "end": v(-0.85, 3.05) * mm});
            skLineSegment(sketch, "E349", {"start": v(-0.85, 3.05) * mm, "end": v(-1.05, 2.84) * mm});
            skLineSegment(sketch, "E350", {"start": v(-1.05, 2.84) * mm, "end": v(-1.05, 3.2) * mm});
            skLineSegment(sketch, "E351", {"start": v(-1.05, 3.2) * mm, "end": v(-2.06, 2.57) * mm});
            skLineSegment(sketch, "E352", {"start": v(-2.06, 2.57) * mm, "end": v(-1.63, 2.51) * mm});
            skLineSegment(sketch, "E353", {"start": v(-1.63, 2.51) * mm, "end": v(-2.71, 2.22) * mm});
            skLineSegment(sketch, "E354", {"start": v(-2.9, 2.5) * mm, "end": v(-3.5, 1.76) * mm});
            skLineSegment(sketch, "E355", {"start": v(-3.5, 1.76) * mm, "end": v(-2.71, 2.22) * mm});
            skLineSegment(sketch, "E356", {"start": v(-0.87, 3.4) * mm, "end": v(-0.73, 3.42) * mm});
            skLineSegment(sketch, "E357", {"start": v(-0.73, 3.42) * mm, "end": v(-0.66, 3.34) * mm});
            skLineSegment(sketch, "E358", {"start": v(-0.66, 3.34) * mm, "end": v(-0.7, 3.23) * mm});
            skLineSegment(sketch, "E359", {"start": v(-0.7, 3.23) * mm, "end": v(-0.86, 3.2) * mm});
            skLineSegment(sketch, "E360", {"start": v(-0.86, 3.2) * mm, "end": v(-0.99, 3.28) * mm});
            skLineSegment(sketch, "E361", {"start": v(-0.99, 3.28) * mm, "end": v(-0.87, 3.4) * mm});
            skLineSegment(sketch, "E362", {"start": v(2.99, -2.27) * mm, "end": v(2.44, -2.76) * mm});
            skLineSegment(sketch, "E363", {"start": v(2.44, -2.76) * mm, "end": v(2.52, -2.45) * mm});
            skLineSegment(sketch, "E364", {"start": v(2.52, -2.45) * mm, "end": v(1.71, -2.93) * mm});
            skLineSegment(sketch, "E365", {"start": v(1.71, -2.93) * mm, "end": v(1.81, -2.65) * mm});
            skLineSegment(sketch, "E366", {"start": v(1.81, -2.65) * mm, "end": v(1.18, -3.01) * mm});
            skLineSegment(sketch, "E367", {"start": v(1.18, -3.01) * mm, "end": v(1.4, -3.07) * mm});
            skLineSegment(sketch, "E368", {"start": v(1.4, -3.07) * mm, "end": v(1.18, -3.19) * mm});
            skLineSegment(sketch, "E369", {"start": v(1.18, -3.19) * mm, "end": v(1.28, -3.38) * mm});
            skLineSegment(sketch, "E370", {"start": v(1.28, -3.38) * mm, "end": v(1, -3.25) * mm});
            skLineSegment(sketch, "E371", {"start": v(1, -3.25) * mm, "end": v(0.8, -3.52) * mm});
            skLineSegment(sketch, "E372", {"start": v(0.8, -3.52) * mm, "end": v(0.74, -3.23) * mm});
            skLineSegment(sketch, "E373", {"start": v(0.74, -3.23) * mm, "end": v(0.4, -3.12) * mm});
            skLineSegment(sketch, "E374", {"start": v(0.4, -3.12) * mm, "end": v(0.66, -2.95) * mm});
            skLineSegment(sketch, "E375", {"start": v(0.66, -2.95) * mm, "end": v(0.6, -2.64) * mm});
            skLineSegment(sketch, "E376", {"start": v(0.6, -2.64) * mm, "end": v(0.94, -2.8) * mm});
            skLineSegment(sketch, "E377", {"start": v(0.94, -2.8) * mm, "end": v(1.14, -2.6) * mm});
            skLineSegment(sketch, "E378", {"start": v(1.14, -2.6) * mm, "end": v(1.14, -2.96) * mm});
            skLineSegment(sketch, "E379", {"start": v(1.14, -2.96) * mm, "end": v(2.16, -2.33) * mm});
            skLineSegment(sketch, "E380", {"start": v(2.16, -2.33) * mm, "end": v(1.72, -2.27) * mm});
            skLineSegment(sketch, "E381", {"start": v(1.72, -2.27) * mm, "end": v(2.8, -1.98) * mm});
            skLineSegment(sketch, "E382", {"start": v(2.99, -2.27) * mm, "end": v(3.6, -1.52) * mm});
            skLineSegment(sketch, "E383", {"start": v(3.6, -1.52) * mm, "end": v(2.8, -1.98) * mm});
            skLineSegment(sketch, "E384", {"start": v(0.96, -3.16) * mm, "end": v(0.83, -3.18) * mm});
            skLineSegment(sketch, "E385", {"start": v(0.83, -3.18) * mm, "end": v(0.76, -3.1) * mm});
            skLineSegment(sketch, "E386", {"start": v(0.76, -3.1) * mm, "end": v(0.8, -2.99) * mm});
            skLineSegment(sketch, "E387", {"start": v(0.8, -2.99) * mm, "end": v(0.95, -2.96) * mm});
            skLineSegment(sketch, "E388", {"start": v(0.95, -2.96) * mm, "end": v(1.08, -3.04) * mm});
            skLineSegment(sketch, "E389", {"start": v(1.08, -3.04) * mm, "end": v(0.96, -3.16) * mm});
            skLineSegment(sketch, "E390", {"start": v(-1.53, 1.98) * mm, "end": v(-0.97, 1.46) * mm});
            skLineSegment(sketch, "E391", {"start": v(-0.97, 1.46) * mm, "end": v(0.64, 1.46) * mm});
            skLineSegment(sketch, "E392", {"start": v(0.64, 1.46) * mm, "end": v(1.2, 2.08) * mm});
            skLineSegment(sketch, "E393", {"start": v(1.2, 2.08) * mm, "end": v(-1.53, 1.98) * mm});
            skLineSegment(sketch, "E394", {"start": v(-1.53, 1.98) * mm, "end": v(-1.53, 0) * mm});
            skLineSegment(sketch, "E395", {"start": v(-1.53, 0) * mm, "end": v(-0.7, 0) * mm});
            skLineSegment(sketch, "E396", {"start": v(-0.7, 0) * mm, "end": v(-0.97, 1.46) * mm});
            skLineSegment(sketch, "E397", {"start": v(-0.7, 0) * mm, "end": v(0.44, -0.43) * mm});
            skLineSegment(sketch, "E398", {"start": v(0.44, -0.43) * mm, "end": v(1.08, -1.6) * mm});
            skLineSegment(sketch, "E399", {"start": v(1.08, -1.6) * mm, "end": v(0.17, -2.35) * mm});
            skLineSegment(sketch, "E400", {"start": v(0.17, -2.35) * mm, "end": v(-1.53, -2.35) * mm});
            skLineSegment(sketch, "E401", {"start": v(-1.53, -2.35) * mm, "end": v(-1.53, -1.57) * mm});
            skLineSegment(sketch, "E402", {"start": v(-1.53, -1.57) * mm, "end": v(0, -1.37) * mm});
            skLineSegment(sketch, "E403", {"start": v(0, -1.37) * mm, "end": v(-1.53, 0) * mm});
            skSolve(sketch);
        }
        {
            var Q0;
            Q0=makeQuery(id+"F14.imprint","IMPRINT",FACE,{"disambiguationData":[TD([[makeQuery(id+"F14.imprint","IMPRINT",EDGE,{"derivedFrom":sQuery(id+"F14.wireOp",EDGE,"E333.0")}),1.0]])]});
            var Q1;
            Q1=makeQuery(id+"F14.imprint","IMPRINT",FACE,{"disambiguationData":[TD([[makeQuery(id+"F14.imprint","IMPRINT",EDGE,{"derivedFrom":sQuery(id+"F14.wireOp",EDGE,"E356")}),-1.0]])]});
            var Q2;
            Q2=makeQuery(id+"F14.imprint","IMPRINT",FACE,{"disambiguationData":[TD([[makeQuery(id+"F14.imprint","IMPRINT",EDGE,{"derivedFrom":sQuery(id+"F14.wireOp",EDGE,"E384")}),-1.0]])]});
            extrude(context, id + "F15", {"entities" : qUnion([Q0, Q1, Q2]), "operationType" : NewBodyOperationType.REMOVE, "oppositeDirection" : true, "depth" : 1 * mm, "offsetDistance" : 25.4 * mm});
        }
    });
